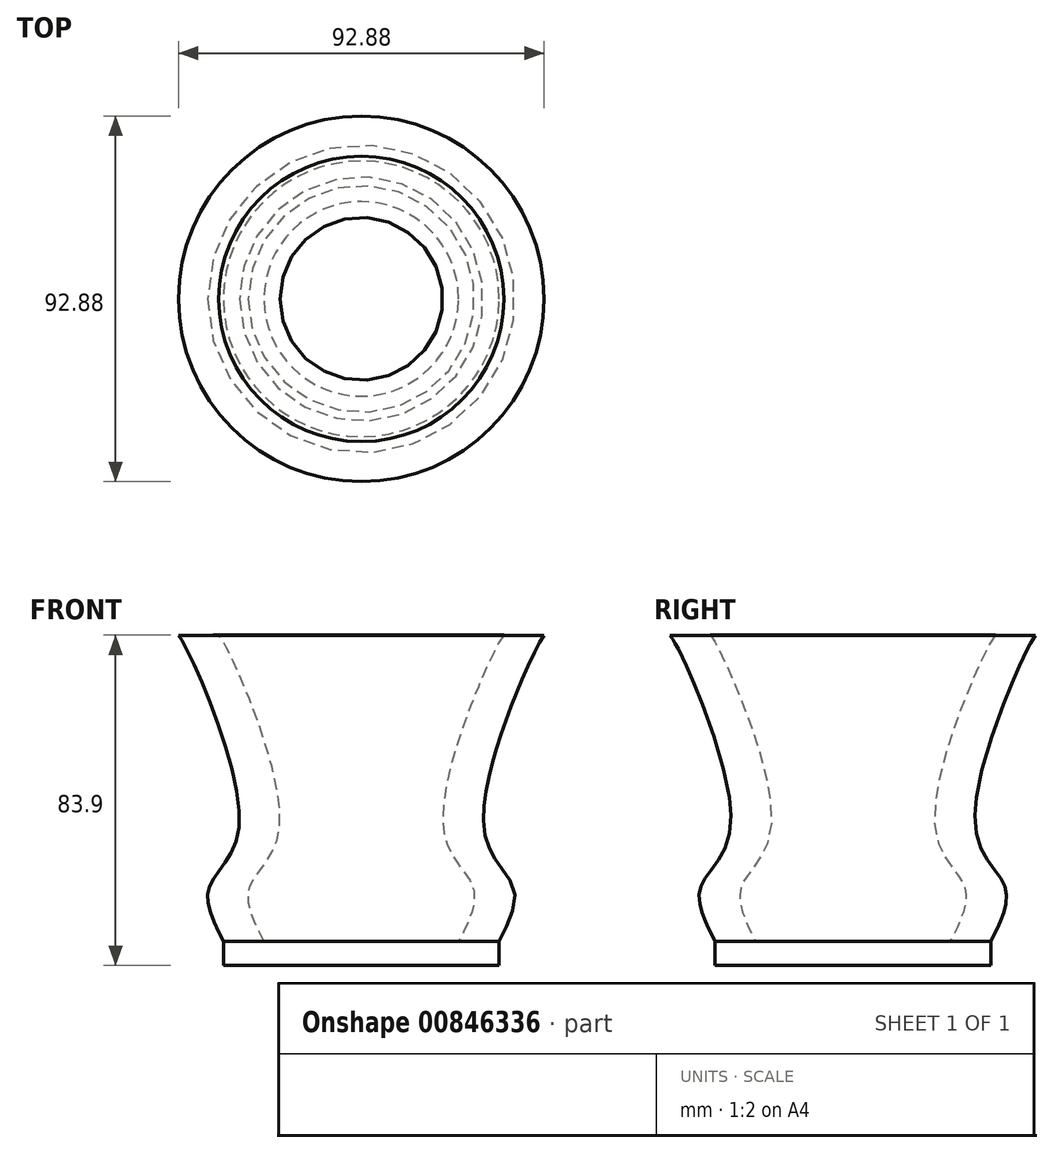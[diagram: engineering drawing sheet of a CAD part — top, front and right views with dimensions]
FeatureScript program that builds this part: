
annotation { "Feature Type Name" : "Feature", "Feature Type Description" : "" }
export const myFeature = defineFeature(function(context is Context, id is Id, definition is map)
    precondition{}
    {
        {
            var Q0;
            Q0=qCreatedBy(makeId("Front.planeOp"),FACE);
            var sketch = newSketch(context, id + "F0", { "sketchPlane" : qUnion([Q0])});
            skFitSpline(sketch, "E0", {"points": [v(-35.01, 0) * mm, v(-38.77, 13.54) * mm, v(-31, 30.45) * mm, v(-46.54, 77.84) * mm, v(-46.73, 77.65) * mm], "startDerivative": vector(-30.66, 60.57) * mm, "endDerivative": vector(-3.64, -10.88) * mm});
            skFitSpline(sketch, "E1", {"points": [v(-24.71, 0) * mm, v(-28.47, 13.54) * mm, v(-20.7, 30.45) * mm, v(-36.24, 77.84) * mm, v(-36.43, 77.65) * mm], "startDerivative": vector(-30.66, 60.57) * mm, "endDerivative": vector(-3.64, -10.88) * mm});
            skLineSegment(sketch, "E2", {"start": v(-35.01, 0) * mm, "end": v(-35.01, -6.06) * mm});
            skLineSegment(sketch, "E3", {"start": v(-35.01, -6.06) * mm, "end": v(0, -6.06) * mm});
            skLineSegment(sketch, "E4", {"start": v(0, -6.06) * mm, "end": v(0, 0) * mm});
            skLineSegment(sketch, "E5", {"start": v(0, 0) * mm, "end": v(-24.71, 0) * mm});
            skLineSegment(sketch, "E6", {"start": v(-46.7, 77.77) * mm, "end": v(-36.24, 77.84) * mm});
            skLineSegment(sketch, "E7", {"start": v(0, 0) * mm, "end": v(0, 20.56) * mm});
            skSolve(sketch);
        }
        {
            var Q0;
            {var subQ0=sQuery(id+"F0.wireOp",EDGE,"E2");Q0=makeQuery(id+"F0.imprint","IMPRINT",FACE,{"disambiguationData":[TD([[makeQuery(id+"F0.imprint","IMPRINT",EDGE,{"derivedFrom":subQ0}),1.0]])]});}
            var Q1;
            Q1=sQuery(id+"F0.wireOp",EDGE,"E7");
            revolve(context, id + "F1", {"surfaceOperationType" : NewSurfaceOperationType.NEW, "entities" : qUnion([Q0]), "axis" : qUnion([Q1]), "revolveType" : RevolveType.FULL});
        }
    });
